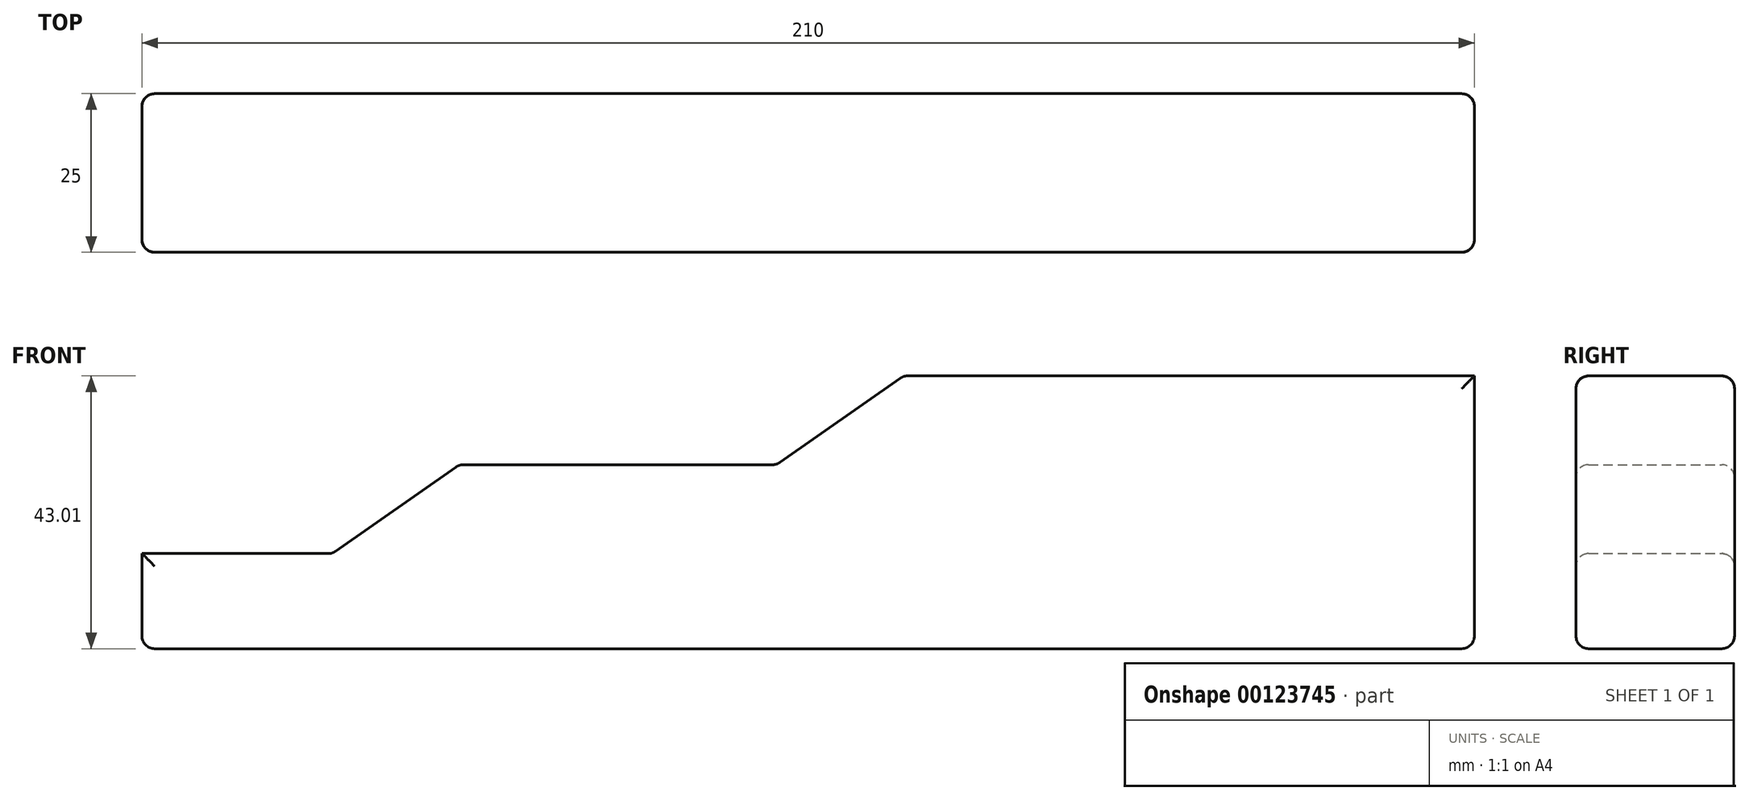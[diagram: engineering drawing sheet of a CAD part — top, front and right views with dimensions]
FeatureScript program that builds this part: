
annotation { "Feature Type Name" : "Feature", "Feature Type Description" : "" }
export const myFeature = defineFeature(function(context is Context, id is Id, definition is map)
    precondition{}
    {
        {
            var Q0;
            Q0=qCreatedBy(makeId("Front.planeOp"),FACE);
            var sketch = newSketch(context, id + "F0", { "sketchPlane" : qUnion([Q0])});
            skLineSegment(sketch, "E0", {"start": v(0, 0) * mm, "end": v(0, 15) * mm});
            skLineSegment(sketch, "E1", {"start": v(0, 15) * mm, "end": v(30, 15) * mm});
            skLineSegment(sketch, "E2", {"start": v(30, 15) * mm, "end": v(50, 29) * mm});
            skLineSegment(sketch, "E3", {"start": v(50, 29) * mm, "end": v(100, 29) * mm});
            skLineSegment(sketch, "E4", {"start": v(100, 29) * mm, "end": v(120, 43) * mm});
            skLineSegment(sketch, "E5", {"start": v(120, 43) * mm, "end": v(210, 43) * mm});
            skLineSegment(sketch, "E6", {"start": v(0, 0) * mm, "end": v(210, 0) * mm});
            skLineSegment(sketch, "E7", {"start": v(210, 43) * mm, "end": v(210, 0) * mm});
            skSolve(sketch);
        }
        {
            var Q0;
            Q0 = qSketchRegion(id + "F0", true);
            extrude(context, id + "F1", {"entities" : qUnion([Q0]), "depth" : 25 * mm});
        }
        {
            var Q0;
            Q0=makeQuery(id+"F1.opExtrude","CAP_EDGE",EDGE,{"disambiguationData":[OSD([sQuery(id+"F0.wireOp",EDGE,"E5")])],"isStart":false});
            var Q1;
            Q1=makeQuery(id+"F1.opExtrude","CAP_EDGE",EDGE,{"disambiguationData":[OSD([sQuery(id+"F0.wireOp",EDGE,"E5")])],"isStart":true});
            var Q2;
            Q2=makeQuery(id+"F1.opExtrude","CAP_EDGE",EDGE,{"disambiguationData":[OSD([sQuery(id+"F0.wireOp",EDGE,"E7")])],"isStart":false});
            var Q3;
            Q3=makeQuery(id+"F1.opExtrude","CAP_EDGE",EDGE,{"disambiguationData":[OSD([sQuery(id+"F0.wireOp",EDGE,"E7")])],"isStart":true});
            var Q4;
            Q4=makeQuery(id+"F1.opExtrude","SWEPT_EDGE",EDGE,{"disambiguationData":[OSD([sQuery(id+"F0.wireOp",EDGE,"E6"),sQuery(id+"F0.wireOp",EDGE,"E7")])]});
            var Q5;
            Q5=makeQuery(id+"F1.opExtrude","CAP_EDGE",EDGE,{"disambiguationData":[OSD([sQuery(id+"F0.wireOp",EDGE,"E6")])],"isStart":false});
            var Q6;
            Q6=makeQuery(id+"F1.opExtrude","CAP_EDGE",EDGE,{"disambiguationData":[OSD([sQuery(id+"F0.wireOp",EDGE,"E4")])],"isStart":false});
            var Q7;
            Q7=makeQuery(id+"F1.opExtrude","CAP_EDGE",EDGE,{"disambiguationData":[OSD([sQuery(id+"F0.wireOp",EDGE,"E3")])],"isStart":false});
            var Q8;
            Q8=makeQuery(id+"F1.opExtrude","CAP_EDGE",EDGE,{"disambiguationData":[OSD([sQuery(id+"F0.wireOp",EDGE,"E2")])],"isStart":false});
            var Q9;
            Q9=makeQuery(id+"F1.opExtrude","CAP_EDGE",EDGE,{"disambiguationData":[OSD([sQuery(id+"F0.wireOp",EDGE,"E1")])],"isStart":false});
            var Q10;
            Q10=makeQuery(id+"F1.opExtrude","CAP_EDGE",EDGE,{"disambiguationData":[OSD([sQuery(id+"F0.wireOp",EDGE,"E1")])],"isStart":true});
            var Q11;
            Q11=makeQuery(id+"F1.opExtrude","SWEPT_EDGE",EDGE,{"disambiguationData":[OSD([sQuery(id+"F0.wireOp",EDGE,"E1"),sQuery(id+"F0.wireOp",EDGE,"E2")])]});
            var Q12;
            Q12=makeQuery(id+"F1.opExtrude","CAP_EDGE",EDGE,{"disambiguationData":[OSD([sQuery(id+"F0.wireOp",EDGE,"E2")])],"isStart":true});
            var Q13;
            Q13=makeQuery(id+"F1.opExtrude","SWEPT_EDGE",EDGE,{"disambiguationData":[OSD([sQuery(id+"F0.wireOp",EDGE,"E2"),sQuery(id+"F0.wireOp",EDGE,"E3")])]});
            var Q14;
            Q14=makeQuery(id+"F1.opExtrude","CAP_EDGE",EDGE,{"disambiguationData":[OSD([sQuery(id+"F0.wireOp",EDGE,"E3")])],"isStart":true});
            var Q15;
            Q15=makeQuery(id+"F1.opExtrude","CAP_EDGE",EDGE,{"disambiguationData":[OSD([sQuery(id+"F0.wireOp",EDGE,"E4")])],"isStart":true});
            var Q16;
            Q16=makeQuery(id+"F1.opExtrude","SWEPT_EDGE",EDGE,{"disambiguationData":[OSD([sQuery(id+"F0.wireOp",EDGE,"E3"),sQuery(id+"F0.wireOp",EDGE,"E4")])]});
            var Q17;
            Q17=makeQuery(id+"F1.opExtrude","SWEPT_EDGE",EDGE,{"disambiguationData":[OSD([sQuery(id+"F0.wireOp",EDGE,"E4"),sQuery(id+"F0.wireOp",EDGE,"E5")])]});
            var Q18;
            Q18=makeQuery(id+"F1.opExtrude","CAP_EDGE",EDGE,{"disambiguationData":[OSD([sQuery(id+"F0.wireOp",EDGE,"E0")])],"isStart":true});
            var Q19;
            Q19=makeQuery(id+"F1.opExtrude","SWEPT_EDGE",EDGE,{"disambiguationData":[OSD([sQuery(id+"F0.wireOp",EDGE,"E0"),sQuery(id+"F0.wireOp",EDGE,"E6")])]});
            var Q20;
            Q20=makeQuery(id+"F1.opExtrude","CAP_EDGE",EDGE,{"disambiguationData":[OSD([sQuery(id+"F0.wireOp",EDGE,"E0")])],"isStart":false});
            var Q21;
            Q21=makeQuery(id+"F1.opExtrude","CAP_EDGE",EDGE,{"disambiguationData":[OSD([sQuery(id+"F0.wireOp",EDGE,"E6")])],"isStart":true});
            fillet(context, id + "F2", {"entities" : qUnion([Q0, Q1, Q2, Q3, Q4, Q5, Q6, Q7, Q8, Q9, Q10, Q11, Q12, Q13, Q14, Q15, Q16, Q17, Q18, Q19, Q20, Q21]), "radius" : 2 * mm, "tangentPropagation" : true, "allowEdgeOverflow" : false});
        }
    });
